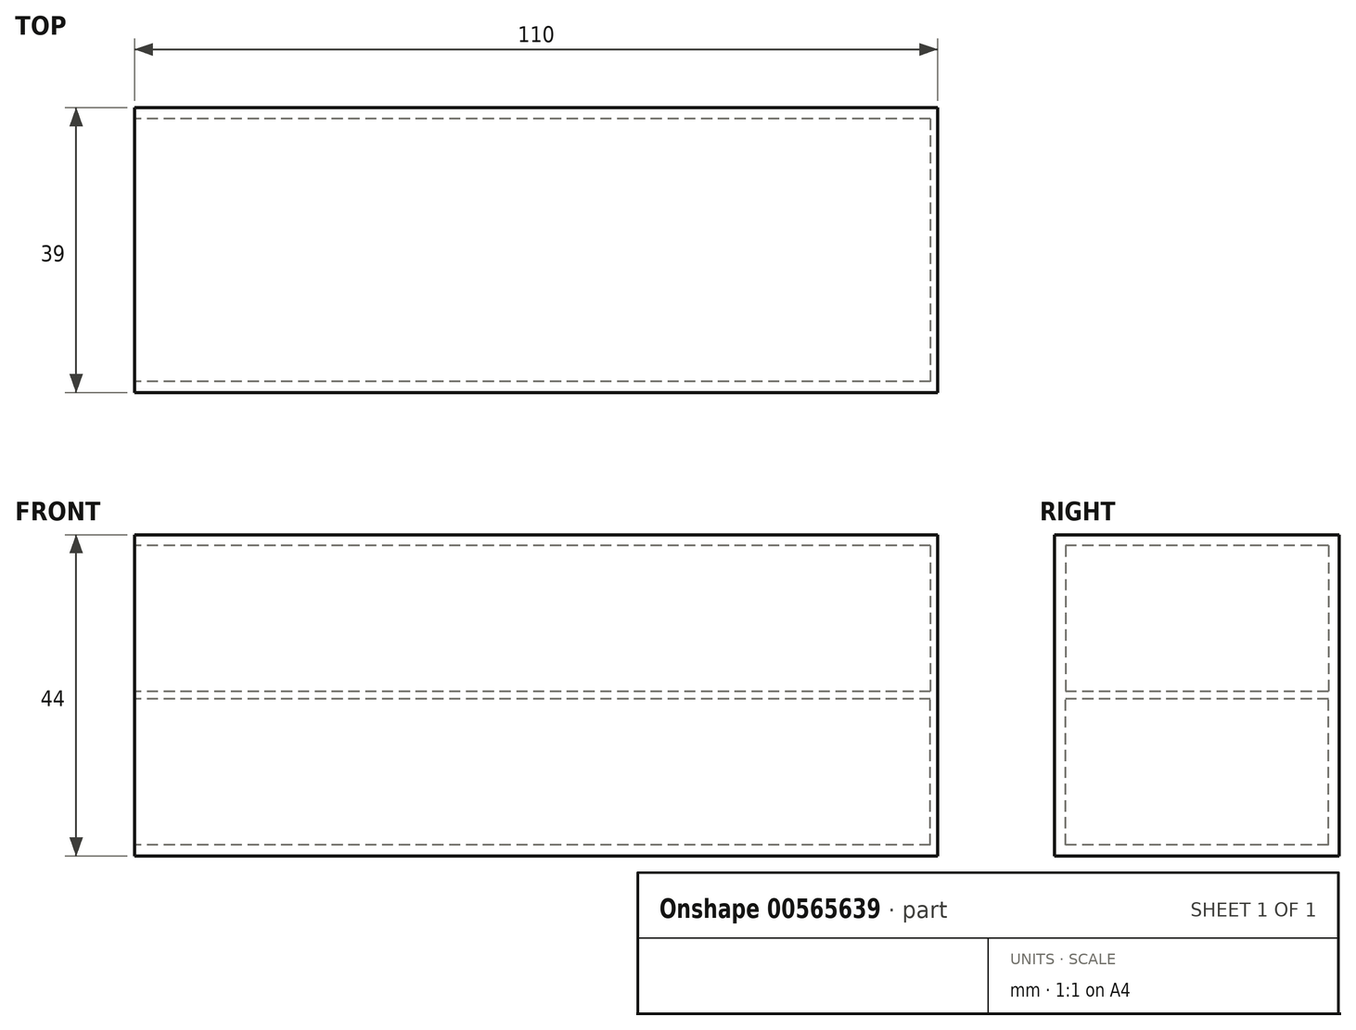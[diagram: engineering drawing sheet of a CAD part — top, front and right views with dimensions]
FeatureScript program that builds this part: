
annotation { "Feature Type Name" : "Feature", "Feature Type Description" : "" }
export const myFeature = defineFeature(function(context is Context, id is Id, definition is map)
    precondition{}
    {
        {
            var Q0;
            Q0=qCreatedBy(makeId("Front.planeOp"),FACE);
            var sketch = newSketch(context, id + "F0", { "sketchPlane" : qUnion([Q0])});
            skLineSegment(sketch, "E0.bottom", {"start": v(55, 22) * mm, "end": v(-55, 22) * mm});
            skLineSegment(sketch, "E0.top", {"start": v(55, -22) * mm, "end": v(-55, -22) * mm});
            skLineSegment(sketch, "E0.left", {"start": v(55, 22) * mm, "end": v(55, -22) * mm});
            skLineSegment(sketch, "E0.right", {"start": v(-55, 22) * mm, "end": v(-55, -22) * mm});
            skPoint(sketch, "E0.middle", {"position": v(0, 0) * mm});
            skSolve(sketch);
        }
        {
            var Q0;
            Q0=makeQuery(id+"F0.imprint","IMPRINT",FACE,{"disambiguationData":[TD([[makeQuery(id+"F0.imprint","IMPRINT",EDGE,{"derivedFrom":sQuery(id+"F0.wireOp",EDGE,"E0.bottom")}),1.0]])]});
            extrude(context, id + "F1", {"entities" : qUnion([Q0]), "depth" : 39 * mm, "offsetDistance" : 25 * mm});
        }
        {
            var Q0;
            Q0=makeQuery(id+"F1.opExtrude","SWEPT_FACE",FACE,{"disambiguationData":[OSD([sQuery(id+"F0.wireOp",EDGE,"E0.right")])]});
            var sketch = newSketch(context, id + "F2", { "sketchPlane" : qUnion([Q0])});
            skLineSegment(sketch, "E1", {"start": v(1.5, 10.5) * mm, "end": v(37.5, 10.5) * mm, "construction": true});
            skLineSegment(sketch, "E2", {"start": v(1.5, 10.5) * mm, "end": v(0, 10.5) * mm, "construction": true});
            skLineSegment(sketch, "E3", {"start": v(37.5, 10.5) * mm, "end": v(39, 10.5) * mm, "construction": true});
            skLineSegment(sketch, "E4", {"start": v(39, 10.5) * mm, "end": v(39, 22) * mm, "construction": true});
            skLineSegment(sketch, "E5.bottom", {"start": v(0, 0.5) * mm, "end": v(39, 0.5) * mm, "construction": true});
            skLineSegment(sketch, "E6", {"start": v(39, 10.5) * mm, "end": v(39, 0.5) * mm, "construction": true});
            skLineSegment(sketch, "E7", {"start": v(19.5, 0.5) * mm, "end": v(19.5, 20.5) * mm, "construction": true});
            skPoint(sketch, "E8", {"position": v(19.5, 10.5) * mm});
            skLineSegment(sketch, "E9.bottom", {"start": v(1.5, 20.5) * mm, "end": v(37.5, 20.5) * mm});
            skLineSegment(sketch, "E9.top", {"start": v(1.5, 0.5) * mm, "end": v(37.5, 0.5) * mm});
            skLineSegment(sketch, "E9.left", {"start": v(1.5, 20.5) * mm, "end": v(1.5, 0.5) * mm});
            skLineSegment(sketch, "E9.right", {"start": v(37.5, 20.5) * mm, "end": v(37.5, 0.5) * mm});
            skLineSegment(sketch, "E10", {"start": v(0, 0) * mm, "end": v(39, 0) * mm, "construction": true});
            skLineSegment(sketch, "E11.MirrorCS", {"start": v(37.5, -10.5) * mm, "end": v(39, -10.5) * mm, "construction": true});
            skLineSegment(sketch, "E12.MirrorCS", {"start": v(1.5, -10.5) * mm, "end": v(0, -10.5) * mm, "construction": true});
            skPoint(sketch, "E13.MirrorP", {"position": v(19.5, -10.5) * mm});
            skLineSegment(sketch, "E14.MirrorCS", {"start": v(1.5, -0.5) * mm, "end": v(37.5, -0.5) * mm});
            skLineSegment(sketch, "E15.MirrorCS", {"start": v(0, -0.5) * mm, "end": v(39, -0.5) * mm, "construction": true});
            skLineSegment(sketch, "E16.MirrorCS", {"start": v(1.5, -20.5) * mm, "end": v(1.5, -0.5) * mm});
            skLineSegment(sketch, "E17.MirrorCS", {"start": v(37.5, -20.5) * mm, "end": v(37.5, -0.5) * mm});
            skLineSegment(sketch, "E18.MirrorCS", {"start": v(39, -10.5) * mm, "end": v(39, -0.5) * mm, "construction": true});
            skLineSegment(sketch, "E19.MirrorCS", {"start": v(19.5, -0.5) * mm, "end": v(19.5, -20.5) * mm, "construction": true});
            skLineSegment(sketch, "E20.MirrorCS", {"start": v(1.5, -20.5) * mm, "end": v(37.5, -20.5) * mm});
            skLineSegment(sketch, "E21.MirrorCS", {"start": v(39, -10.5) * mm, "end": v(39, -22) * mm, "construction": true});
            skLineSegment(sketch, "E22.MirrorCS", {"start": v(1.5, -10.5) * mm, "end": v(37.5, -10.5) * mm, "construction": true});
            skLineSegment(sketch, "E23.bottom", {"start": v(0, -22) * mm, "end": v(-5, -22) * mm});
            skLineSegment(sketch, "E23.top", {"start": v(0, -9.3) * mm, "end": v(-5, -9.3) * mm});
            skLineSegment(sketch, "E23.left", {"start": v(0, -22) * mm, "end": v(0, -9.3) * mm});
            skLineSegment(sketch, "E23.right", {"start": v(-5, -22) * mm, "end": v(-5, -9.3) * mm});
            skLineSegment(sketch, "E24.bottom", {"start": v(39, -22) * mm, "end": v(44, -22) * mm});
            skLineSegment(sketch, "E24.top", {"start": v(39, -9.3) * mm, "end": v(44, -9.3) * mm});
            skLineSegment(sketch, "E24.left", {"start": v(39, -22) * mm, "end": v(39, -9.3) * mm});
            skLineSegment(sketch, "E24.right", {"start": v(44, -22) * mm, "end": v(44, -9.3) * mm});
            skLineSegment(sketch, "E25.top", {"start": v(39, 17.38) * mm, "end": v(44, 17.38) * mm});
            skLineSegment(sketch, "E25.left", {"start": v(39, 22) * mm, "end": v(39, 17.38) * mm});
            skSolve(sketch);
        }
        {
            var Q0;
            Q0=makeQuery(id+"F2.imprint","IMPRINT",FACE,{"disambiguationData":[TD([[makeQuery(id+"F2.imprint","IMPRINT",EDGE,{"derivedFrom":sQuery(id+"F2.wireOp",EDGE,"E9.bottom")}),-1.0]])]});
            var Q1;
            Q1=makeQuery(id+"F2.imprint","IMPRINT",FACE,{"disambiguationData":[TD([[makeQuery(id+"F2.imprint","IMPRINT",EDGE,{"derivedFrom":sQuery(id+"F2.wireOp",EDGE,"E14.MirrorCS")}),-1.0]])]});
            extrude(context, id + "F3", {"entities" : qUnion([Q0, Q1]), "operationType" : NewBodyOperationType.REMOVE, "oppositeDirection" : true, "depth" : 109 * mm, "offsetDistance" : 25 * mm});
        }
    });
